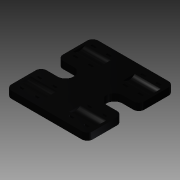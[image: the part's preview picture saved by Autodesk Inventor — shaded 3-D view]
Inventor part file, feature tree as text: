
AUTODESK INVENTOR PART (.ipt)
format: ipt  version: 2013 (Build 170138000, 138)  size: 232,448 bytes
history: native  units: mm
features: extrude x5, sketch x5, mirror x2, fillet x2, projected_geometry x1
ambient origin geometry x8: Origin, YZ Plane, XZ Plane, XY Plane, X Axis, Y Axis, Z Axis, Center Point
bodies: Solid1 (feature_tree)
feature tree (15):
  extrude  "Extrusion1"  Depth=80.0mm
  extrude  "Extrusion2"  Depth=50.0mm
  extrude  "Extrusion3"  Depth=2.5mm
  extrude  "Extrusion4"  Depth=15.0mm
  mirror  "Mirror1"
  mirror  "Mirror2"
  fillet  "Fillet1"  Radius=6.477mm
  extrude  "Extrusion6"  Depth=6.477mm TaperAngle=0.0deg
  fillet  "Fillet3"  Radius=5.0mm
  sketch  "Sketch1"  dims[d0=75.0mm d2=80.0mm]
  sketch  "Sketch2"  dims[d3=6.477mm d4=0.0mm d5=50.0mm]
  sketch  "Sketch3"  dims[d7=24.0mm d9=2.5mm]
  projected_geometry  "Projected Loop1"
  sketch  "Sketch4"  dims[d10=45.0deg d11=15.0mm d12=6.477mm d13=0.0mm]
  sketch  "Sketch6"  dims[d14=15.0mm d16=6.477mm d17=0.0mm d18=5.0mm d19=15.0mm d20=4.0mm d21=1.5mm d22=6.477mm d23=0.0mm d24=5.0mm d31=7.5mm d33=15.0mm d34=10.0mm d35=0.0mm d36=5.0mm]
